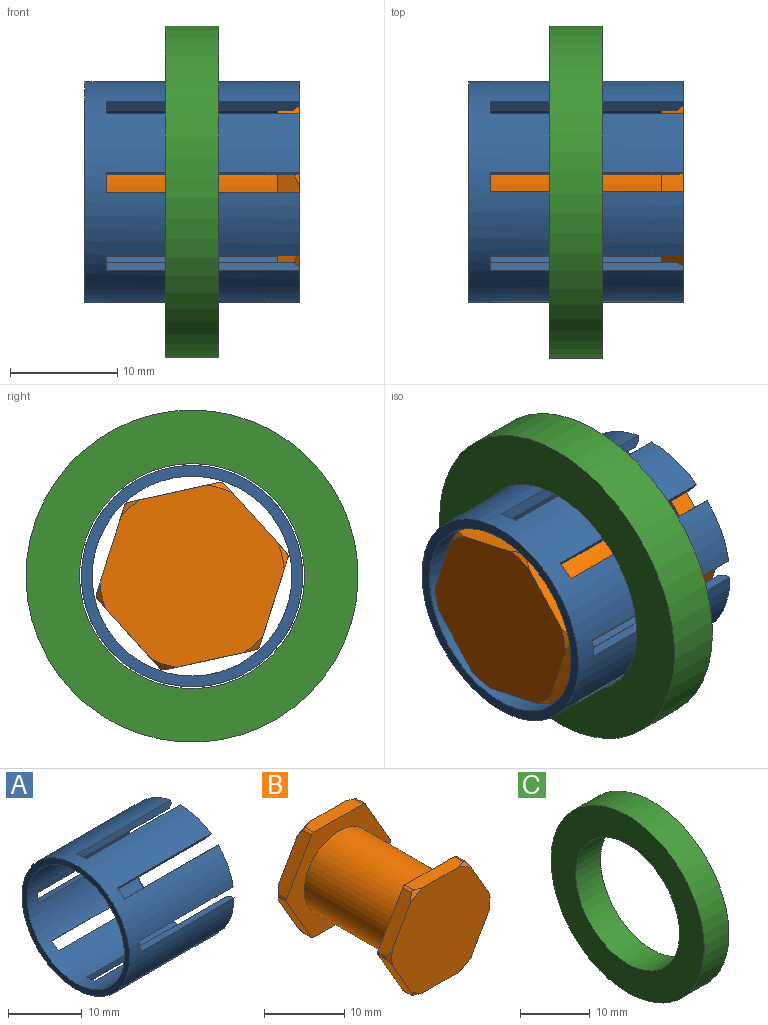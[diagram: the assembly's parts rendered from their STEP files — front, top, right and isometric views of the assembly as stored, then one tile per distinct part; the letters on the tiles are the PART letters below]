
ASSEMBLY  parts=3 mates=2
PART A: 43 faces, bbox 20x20.7x20.7 mm
  f0: cylinder r=9.32mm len=19.5mm, axis (-1,0,0), area 914.7mm2, adj f3,f4,f7,f8,f11,f12,f14,f16
  f1: plane 5.59x3.22mm, normal (1,0,0), area 3.1mm2, adj f3,f17,f20,f40
  f2: plane 5.92x2.28mm, normal (1,0,0), area 3.1mm2, adj f4,f17,f34,f41
  f3: cone r=9.32mm half-angle=45deg, axis (1,0,0), area 4.1mm2, adj f0,f1,f20,f40
  f4: cone r=9.32mm half-angle=45deg, axis (1,0,0), area 4.1mm2, adj f0,f2,f34,f41
  f5: plane 5.59x3.22mm, normal (1,0,0), area 3.1mm2, adj f7,f17,f35,f37
  f6: plane 5.92x2.28mm, normal (1,0,0), area 3.1mm2, adj f8,f17,f22,f38
  f7: cone r=9.32mm half-angle=45deg, axis (1,0,0), area 4.1mm2, adj f0,f5,f35,f37
  f8: cone r=9.32mm half-angle=45deg, axis (1,0,0), area 4.1mm2, adj f0,f6,f22,f38
  f9: plane 5.59x3.22mm, normal (1,0,0), area 3.1mm2, adj f11,f17,f29,f31
  f10: plane 5.92x2.28mm, normal (1,0,0), area 3.1mm2, adj f12,f17,f19,f32
  f11: cone r=9.32mm half-angle=45deg, axis (1,0,0), area 4.1mm2, adj f0,f9,f29,f31
  f12: cone r=9.32mm half-angle=45deg, axis (1,0,0), area 4.1mm2, adj f0,f10,f19,f32
  f13: plane 5.92x2.28mm, normal (1,0,0), area 3.1mm2, adj f14,f17,f26,f28
  f14: cone r=9.32mm half-angle=45deg, axis (1,0,0), area 4.1mm2, adj f0,f13,f26,f28
  f15: plane 5.59x3.22mm, normal (1,0,0), area 3.1mm2, adj f16,f17,f23,f25
  f16: cone r=9.32mm half-angle=45deg, axis (1,0,0), area 4.1mm2, adj f0,f15,f23,f25
  f17: cylinder r=10.33mm len=20.65mm, axis (-1,0,0), area 1038mm2, adj f1,f2,f5,f6,f9,f10,f13,f15
  f18: plane 20.65x20.65mm, normal (-1,0,0), area 61.7mm2, adj f0,f17
  f19: plane 18x1mm, normal (0,1,0), area 17.9mm2, adj f0,f10,f12,f17,f21
  f20: plane 18x0.99mm, normal (0,-0.98,0.17), area 17.9mm2, adj f0,f1,f3,f17,f21
  f21: plane 1.79x1.14mm, normal (1,0,0), area 1.7mm2, adj f0,f17,f19,f20
  f22: plane 18x1mm, normal (0,-1,0), area 17.9mm2, adj f0,f6,f8,f17,f24
  f23: plane 18x0.99mm, normal (0,0.98,-0.17), area 17.9mm2, adj f0,f15,f16,f17,f24
  f24: plane 1.79x1.14mm, normal (1,0,0), area 1.7mm2, adj f0,f17,f22,f23
  f25: plane 18x0.71mm, normal (0,-0.71,0.71), area 17.9mm2, adj f0,f15,f16,f17,f27
  f26: plane 18x0.82mm, normal (0,0.57,-0.82), area 17.9mm2, adj f0,f13,f14,f17,f27
  f27: plane 1.95x1.86mm, normal (1,0,0), area 1.7mm2, adj f0,f17,f25,f26
  f28: plane 18x1mm, normal (0,0,1), area 17.9mm2, adj f0,f13,f14,f17,f30
  f29: plane 18x0.99mm, normal (0,-0.17,-0.98), area 17.9mm2, adj f0,f9,f11,f17,f30
  f30: plane 1.79x1.14mm, normal (1,0,0), area 1.7mm2, adj f0,f17,f28,f29
  f31: plane 18x0.71mm, normal (0,0.71,0.71), area 17.9mm2, adj f0,f9,f11,f17,f33
  f32: plane 18x0.82mm, normal (0,-0.82,-0.57), area 17.9mm2, adj f0,f10,f12,f17,f33
  f33: plane 1.95x1.86mm, normal (1,0,0), area 1.7mm2, adj f0,f17,f31,f32
  f34: plane 18x1mm, normal (0,0,-1), area 17.9mm2, adj f0,f2,f4,f17,f36
  f35: plane 18x0.99mm, normal (0,0.17,0.98), area 17.9mm2, adj f0,f5,f7,f17,f36
  f36: plane 1.79x1.14mm, normal (1,0,0), area 1.7mm2, adj f0,f17,f34,f35
  f37: plane 18x0.71mm, normal (0,-0.71,-0.71), area 17.9mm2, adj f0,f5,f7,f17,f39
  f38: plane 18x0.82mm, normal (0,0.82,0.57), area 17.9mm2, adj f0,f6,f8,f17,f39
  f39: plane 1.95x1.86mm, normal (1,0,0), area 1.7mm2, adj f0,f17,f37,f38
  f40: plane 18x0.71mm, normal (0,0.71,-0.71), area 17.9mm2, adj f0,f1,f3,f17,f42
  f41: plane 18x0.82mm, normal (0,-0.57,0.82), area 17.9mm2, adj f0,f2,f4,f17,f42
  f42: plane 1.95x1.86mm, normal (1,0,0), area 1.7mm2, adj f0,f17,f40,f41
PART B: 52 faces, bbox 18.4x20.7x16.9 mm
  f0: cone r=8.89mm half-angle=45deg, axis (0,-1,0), area 1mm2, adj f14,f30,f36,f43
  f1: cylinder r=4.25mm len=15.25mm, axis (0,1,0), area 148.1mm2, adj f2,f3,f6,f7,f15,f18,f29,f48
  f2: bspline ~10.87x10.8mm, area 85.4mm2, adj f1,f3,f18,f48
  f3: cone r=4.62mm half-angle=45deg, axis (0,1,0), area 20.8mm2, adj f1,f2,f14,f48
  f4: plane 7.55x4.38mm, normal (0.87,0,0.5), area 16.8mm2, adj f9,f19,f26,f31,f34,f38
  f5: plane 1x0.75mm, normal (-1,0,0), area 0.4mm2, adj f6,f7,f27
  f6: bspline ~10.28x10.27mm, area 100.5mm2, adj f1,f5,f7,f18,f27
  f7: bspline ~10.28x10.27mm, area 100.5mm2, adj f1,f5,f6,f29
  f8: cone r=8.89mm half-angle=45deg, axis (0,1,0), area 1mm2, adj f9,f17,f37,f42
  f9: plane 17.25x16mm, normal (0,-1,0), area 217.5mm2, adj f4,f8,f10,f17,f20,f23,f26,f38
  f10: plane 7.55x4.38mm, normal (0.87,0,-0.5), area 16.8mm2, adj f9,f20,f31,f34,f38,f45
  f11: cone r=8.89mm half-angle=45deg, axis (0,-1,0), area 1mm2, adj f13,f14,f33,f40
  f12: cone r=8.89mm half-angle=45deg, axis (0,-1,0), area 1mm2, adj f13,f14,f28,f35
  f13: plane 8.71x2.05mm, normal (0,0,1), area 16.8mm2, adj f11,f12,f14,f24,f33,f35
  f14: plane 17.25x16mm, normal (0,1,0), area 138.9mm2, adj f0,f3,f11,f12,f13,f21,f22,f28
  f15: cone r=2.17mm half-angle=59deg, axis (0,1,0), area 66.2mm2, adj f1,f27
  f16: cylinder r=0.5mm len=1.53mm, axis (0,-1,0), area 0.8mm2, adj f21,f24,f30,f41
  f17: plane 7.55x4.38mm, normal (-0.87,0,0.5), area 16.8mm2, adj f8,f9,f34,f37,f39,f49
  f18: bspline ~10.33x10.33mm, area 100.5mm2, adj f1,f2,f6,f29
  f19: cylinder r=0.5mm len=1.53mm, axis (0,-1,0), area 0.8mm2, adj f4,f26,f34,f50
  f20: cone r=8.89mm half-angle=45deg, axis (0,1,0), area 1mm2, adj f9,f10,f45,f47
  f21: cone r=8.89mm half-angle=45deg, axis (0,-1,0), area 1mm2, adj f14,f16,f30,f41
  f22: cone r=8.89mm half-angle=45deg, axis (0,-1,0), area 1mm2, adj f14,f40,f43,f46
  f23: cone r=8.89mm half-angle=45deg, axis (0,1,0), area 1mm2, adj f9,f42,f47,f51
  f24: plane 18.32x16mm, normal (0,-1,0), area 108.5mm2, adj f13,f16,f25,f28,f30,f32,f33,f35
  f25: cylinder r=6mm len=16mm, axis (0,1,0), area 603.2mm2, adj f24,f34
  f26: cone r=8.89mm half-angle=45deg, axis (0,1,0), area 1mm2, adj f4,f9,f19,f50
  f27: extruded ~8.5x7.93mm, area 9.2mm2, adj f5,f6,f15
  f28: plane 7.55x4.38mm, normal (-0.87,0,0.5), area 16.8mm2, adj f12,f14,f24,f32,f35,f44
  f29: bspline ~10.33x10.33mm, area 100.5mm2, adj f1,f7,f18,f48
  f30: plane 8.71x2.05mm, normal (0,0,-1), area 16.8mm2, adj f0,f14,f16,f21,f24,f36
  f31: cylinder r=0.5mm len=1.53mm, axis (0,-1,0), area 0.8mm2, adj f4,f10,f34,f38
  f32: cylinder r=0.5mm len=1.53mm, axis (0,-1,0), area 0.8mm2, adj f24,f28,f41,f44
  f33: cylinder r=0.5mm len=1.53mm, axis (0,-1,0), area 0.8mm2, adj f11,f13,f24,f40
  f34: plane 18.32x16mm, normal (0,1,0), area 108.5mm2, adj f4,f10,f17,f19,f25,f31,f37,f39
  f35: cylinder r=0.5mm len=1.53mm, axis (0,-1,0), area 0.8mm2, adj f12,f13,f24,f28
  f36: cylinder r=0.5mm len=1.53mm, axis (0,-1,0), area 0.8mm2, adj f0,f24,f30,f43
  f37: cylinder r=0.5mm len=1.53mm, axis (0,-1,0), area 0.8mm2, adj f8,f17,f34,f42
  f38: cone r=8.89mm half-angle=45deg, axis (0,1,0), area 1mm2, adj f4,f9,f10,f31
  f39: cylinder r=0.5mm len=1.53mm, axis (0,-1,0), area 0.8mm2, adj f17,f34,f49,f50
  f40: plane 7.55x4.38mm, normal (0.87,0,0.5), area 16.8mm2, adj f11,f14,f22,f24,f33,f46
  f41: plane 7.55x4.38mm, normal (-0.87,0,-0.5), area 16.8mm2, adj f14,f16,f21,f24,f32,f44
  f42: plane 7.55x4.38mm, normal (-0.87,0,-0.5), area 16.8mm2, adj f8,f9,f23,f34,f37,f51
  f43: plane 7.55x4.38mm, normal (0.87,0,-0.5), area 16.8mm2, adj f0,f14,f22,f24,f36,f46
  f44: cone r=8.89mm half-angle=45deg, axis (0,-1,0), area 1mm2, adj f14,f28,f32,f41
  f45: cylinder r=0.5mm len=1.53mm, axis (0,-1,0), area 0.8mm2, adj f10,f20,f34,f47
  f46: cylinder r=0.5mm len=1.53mm, axis (0,-1,0), area 0.8mm2, adj f22,f24,f40,f43
  f47: plane 8.71x2.05mm, normal (0,0,-1), area 16.8mm2, adj f9,f20,f23,f34,f45,f51
  f48: bspline ~10.87x10.8mm, area 61.8mm2, adj f1,f2,f3,f29
  f49: cone r=8.89mm half-angle=45deg, axis (0,1,0), area 1mm2, adj f9,f17,f39,f50
  f50: plane 8.71x2.05mm, normal (0,0,1), area 16.8mm2, adj f9,f19,f26,f34,f39,f49
  f51: cylinder r=0.5mm len=1.53mm, axis (0,-1,0), area 0.8mm2, adj f23,f34,f42,f47
PART C: 4 faces, bbox 5x31x31 mm
  f0: cylinder r=10.5mm len=21mm, axis (-1,0,0), area 329.9mm2, adj f2,f3
  f1: cylinder r=15.5mm len=31mm, axis (-1,0,0), area 486.9mm2, adj f2,f3
  f2: plane 31x31mm, normal (1,0,0), area 408.4mm2, adj f0,f1
  f3: plane 31x31mm, normal (-1,0,0), area 408.4mm2, adj f0,f1
PLACE A t=(-6.53,-1.56,2.65)mm fixed
PLACE B rot(axis=(-0.51,-0.51,-0.7),110.4deg) t=(-125.53,88.96,31.48)mm
PLACE C rot(axis=(-1,0,0),109deg) t=(-9.03,-1.56,2.65)mm
MATE revolute A.f17 <-> B.f0  axis (-1,0,0) through (-6.53,-1.56,2.65)mm
MATE revolute C.f0 <-> A.f17  axis (-1,0,0) through (-6.53,-1.56,2.65)mm
